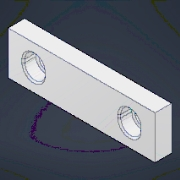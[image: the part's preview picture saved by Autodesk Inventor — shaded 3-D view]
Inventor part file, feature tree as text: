
AUTODESK INVENTOR PART (.ipt)
format: ipt  version: 2024.3 (Build 283343000, 343)  size: 247,296 bytes
history: native  units: mm
features: extrude x5, chamfer x3, sketch x2, fillet x1, projected_geometry x1
ambient origin geometry x8: Origin, YZ Plane, XZ Plane, XY Plane, X Axis, Y Axis, Z Axis, Center Point
bodies: Solid1 (feature_tree)
feature tree (12):
  sketch  "Sketch1"  dims[d0=44.5mm d1=151.0mm]
  extrude  "Extrusion1"  Depth=151.0mm
  extrude  "Extrusion2"  TaperAngle=0.0deg  [1 undecoded]
  extrude  "Extrusion3"  Depth=2.0mm TaperAngle=45.0deg
  chamfer  "Chamfer3"  Distance=14.0mm
  chamfer  "Chamfer4"  Distance=20.7mm
  chamfer  "Chamfer5"  Distance=98.42mm
  sketch  "Sketch2"  dims[d4=22.0mm d5=0.0mm d19=1.0mm d20=2.0mm d21=45.0deg d26=14.0mm d27=20.7mm d28=98.42mm d29=21.0mm d30=1.55mm d31=0.0mm d32=0.0mm d33=16.78mm d34=0.0mm d35=1.5mm d36=2.0mm d37=45.0deg d38=0.5mm d39=2.0mm d40=45.0deg d54=95.0mm d57=45.0deg d59=70.0mm d60=45.0deg d61=85.0mm d62=100.0mm d63=35.0mm d64=0.0mm d65=6.0mm d66=0.0mm d68=2.0mm d69=10.0mm d50=0.5mm d51=0.872665mm d52=0.5mm d53=0.872665mm]
  extrude  "Extrusion6"  Depth=21.0mm
  extrude  "Extrusion7"  Depth=10.0mm
  fillet  "Fillet1"  [1 undecoded]
  projected_geometry  "Projected Loop1"
note: 2 required parameter values undecoded (feature->parameter linkage not recoverable at this tier; creation-order binding heuristic only, values carry confidence <= 0.55)
